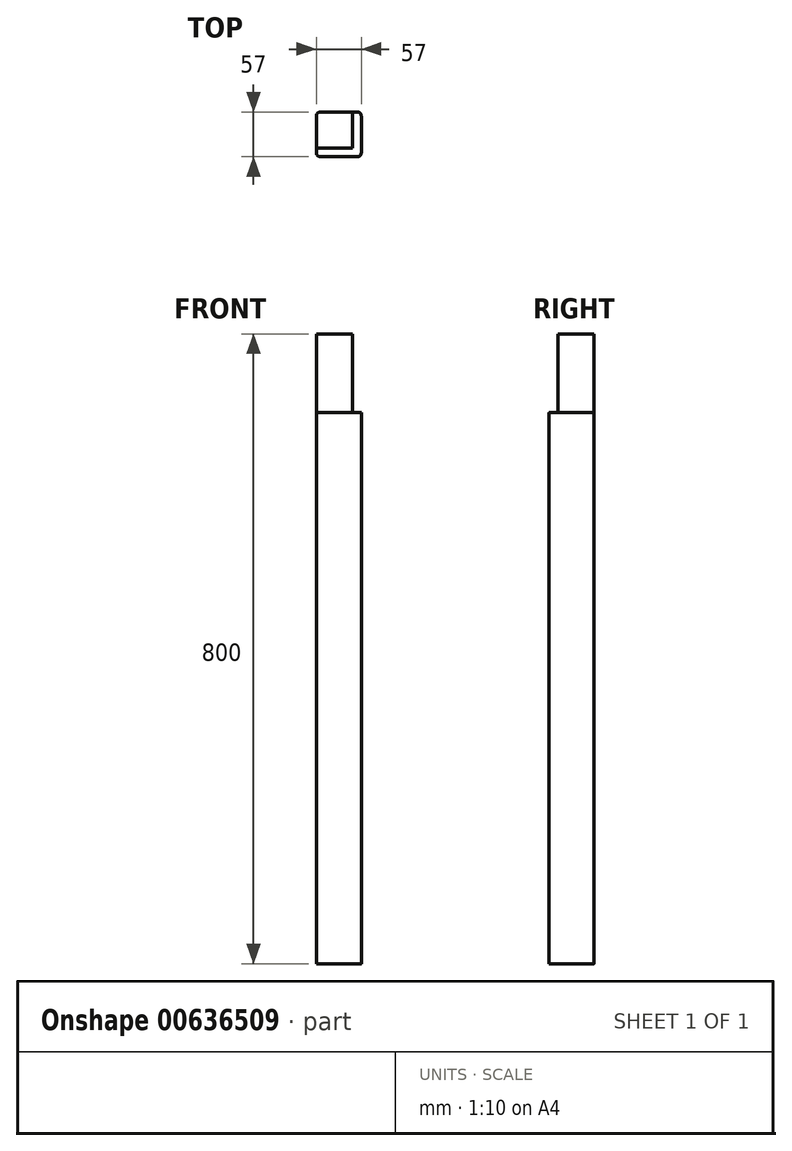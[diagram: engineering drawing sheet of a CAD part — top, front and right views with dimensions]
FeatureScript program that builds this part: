
annotation { "Feature Type Name" : "Feature", "Feature Type Description" : "" }
export const myFeature = defineFeature(function(context is Context, id is Id, definition is map)
    precondition{}
    {
        {
            var Q0;
            Q0=qCreatedBy(makeId("Top.planeOp"),FACE);
            var sketch = newSketch(context, id + "F0", { "sketchPlane" : qUnion([Q0])});
            skLineSegment(sketch, "E0.bottom", {"start": v(-23.5, 28.5) * mm, "end": v(23.5, 28.5) * mm});
            skLineSegment(sketch, "E0.top", {"start": v(-23.5, -28.5) * mm, "end": v(23.5, -28.5) * mm});
            skLineSegment(sketch, "E0.left", {"start": v(-28.5, 23.5) * mm, "end": v(-28.5, -23.5) * mm});
            skLineSegment(sketch, "E0.right", {"start": v(28.5, 23.5) * mm, "end": v(28.5, -23.5) * mm});
            skPoint(sketch, "E1.visualSharp", {"position": v(-28.5, 28.5) * mm});
            skArc(sketch, "E1.filletArc", {"start": v(-23.5, 28.5) * mm, "mid": v(-27.04, 27.04) * mm, "end": v(-28.5, 23.5) * mm});
            skPoint(sketch, "E2.visualSharp", {"position": v(28.5, 28.5) * mm});
            skArc(sketch, "E2.filletArc", {"start": v(28.5, 23.5) * mm, "mid": v(27.04, 27.04) * mm, "end": v(23.5, 28.5) * mm});
            skPoint(sketch, "E3.visualSharp", {"position": v(28.5, -28.5) * mm});
            skArc(sketch, "E3.filletArc", {"start": v(23.5, -28.5) * mm, "mid": v(27.04, -27.04) * mm, "end": v(28.5, -23.5) * mm});
            skPoint(sketch, "E4.visualSharp", {"position": v(-28.5, -28.5) * mm});
            skArc(sketch, "E4.filletArc", {"start": v(-28.5, -23.5) * mm, "mid": v(-27.04, -27.04) * mm, "end": v(-23.5, -28.5) * mm});
            skSolve(sketch);
        }
        {
            var Q0;
            Q0=qSketchRegion(id+"F0",true);
            extrude(context, id + "F1", {"entities" : qUnion([Q0]), "depth" : 800 * mm, "offsetDistance" : 25 * mm});
        }
        {
            var Q0;
            Q0=makeQuery(id+"F1.opExtrude","CAP_FACE",FACE,{"disambiguationData":[OSD([sQuery(id+"F0.wireOp",EDGE,"E0.bottom"),sQuery(id+"F0.wireOp",EDGE,"E0.top"),sQuery(id+"F0.wireOp",EDGE,"E0.left"),sQuery(id+"F0.wireOp",EDGE,"E0.right"),sQuery(id+"F0.wireOp",EDGE,"E1.filletArc"),sQuery(id+"F0.wireOp",EDGE,"E2.filletArc"),sQuery(id+"F0.wireOp",EDGE,"E3.filletArc"),sQuery(id+"F0.wireOp",EDGE,"E4.filletArc")])],"isStart":false});
            var sketch = newSketch(context, id + "F2", { "sketchPlane" : qUnion([Q0])});
            skLineSegment(sketch, "E5.bottom", {"start": v(-35.62, -32.5) * mm, "end": v(32.5, -32.5) * mm});
            skLineSegment(sketch, "E5.top", {"start": v(-35.62, -17.5) * mm, "end": v(17.5, -17.5) * mm});
            skLineSegment(sketch, "E5.left", {"start": v(-35.62, -32.5) * mm, "end": v(-35.62, -17.5) * mm});
            skLineSegment(sketch, "E6", {"start": v(17.5, -17.5) * mm, "end": v(17.5, 34.95) * mm});
            skLineSegment(sketch, "E7", {"start": v(17.5, 34.95) * mm, "end": v(32.5, 34.95) * mm});
            skLineSegment(sketch, "E8", {"start": v(32.5, 34.95) * mm, "end": v(32.5, -32.5) * mm});
            skSolve(sketch);
        }
        {
            var Q0;
            Q0 = qSketchRegion(id + "F2", true);
            extrude(context, id + "F3", {"entities" : qUnion([Q0]), "operationType" : NewBodyOperationType.REMOVE, "oppositeDirection" : true, "depth" : 100 * mm, "offsetDistance" : 25 * mm});
        }
    });
